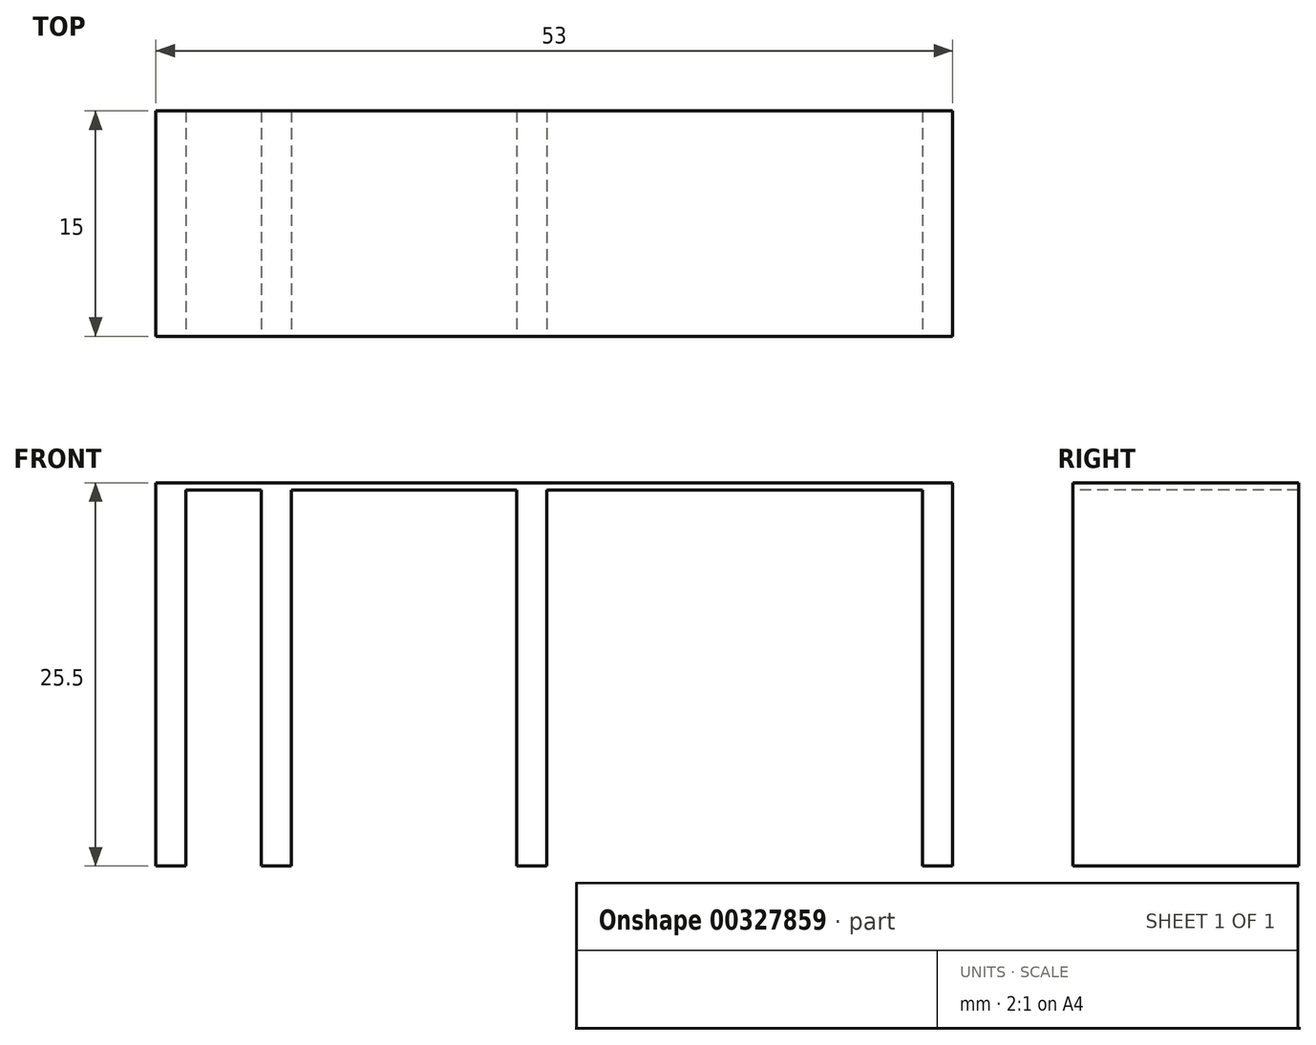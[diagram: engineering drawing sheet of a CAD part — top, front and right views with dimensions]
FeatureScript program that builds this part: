
annotation { "Feature Type Name" : "Feature", "Feature Type Description" : "" }
export const myFeature = defineFeature(function(context is Context, id is Id, definition is map)
    precondition{}
    {
        {
            var Q0;
            Q0=qCreatedBy(makeId("Top.planeOp"),FACE);
            var sketch = newSketch(context, id + "F0", { "sketchPlane" : qUnion([Q0])});
            skLineSegment(sketch, "E0.bottom", {"start": v(-48.72, 7.5) * mm, "end": v(-46.72, 7.5) * mm});
            skLineSegment(sketch, "E0.top", {"start": v(-48.72, -7.5) * mm, "end": v(-46.72, -7.5) * mm});
            skLineSegment(sketch, "E0.left", {"start": v(-48.72, 7.5) * mm, "end": v(-48.72, -7.5) * mm});
            skLineSegment(sketch, "E0.right", {"start": v(-46.72, 7.5) * mm, "end": v(-46.72, -7.5) * mm});
            skLineSegment(sketch, "E1.bottom", {"start": v(-41.72, 7.5) * mm, "end": v(-39.72, 7.5) * mm});
            skLineSegment(sketch, "E1.top", {"start": v(-41.72, -7.5) * mm, "end": v(-39.72, -7.5) * mm});
            skLineSegment(sketch, "E1.left", {"start": v(-41.72, 7.5) * mm, "end": v(-41.72, -7.5) * mm});
            skLineSegment(sketch, "E1.right", {"start": v(-39.72, 7.5) * mm, "end": v(-39.72, -7.5) * mm});
            skLineSegment(sketch, "E2.bottom", {"start": v(-24.72, 7.5) * mm, "end": v(-22.72, 7.5) * mm});
            skLineSegment(sketch, "E2.top", {"start": v(-24.72, -7.5) * mm, "end": v(-22.72, -7.5) * mm});
            skLineSegment(sketch, "E2.left", {"start": v(-24.72, 7.5) * mm, "end": v(-24.72, -7.5) * mm});
            skLineSegment(sketch, "E2.right", {"start": v(-22.72, 7.5) * mm, "end": v(-22.72, -7.5) * mm});
            skLineSegment(sketch, "E3.bottom", {"start": v(2.28, 7.5) * mm, "end": v(4.28, 7.5) * mm});
            skLineSegment(sketch, "E3.top", {"start": v(2.28, -7.5) * mm, "end": v(4.28, -7.5) * mm});
            skLineSegment(sketch, "E3.left", {"start": v(2.28, 7.5) * mm, "end": v(2.28, -7.5) * mm});
            skLineSegment(sketch, "E3.right", {"start": v(4.28, 7.5) * mm, "end": v(4.28, -7.5) * mm});
            skSolve(sketch);
        }
        {
            var Q0;
            Q0 = qSketchRegion(id + "F0", true);
            extrude(context, id + "F1", {"entities" : qUnion([Q0]), "depth" : 25 * mm});
        }
        {
            var Q0;
            Q0=makeQuery(id+"F1.opExtrude","CAP_FACE",FACE,{"disambiguationData":[OSD([sQuery(id+"F0.wireOp",EDGE,"E0.bottom"),sQuery(id+"F0.wireOp",EDGE,"E0.top"),sQuery(id+"F0.wireOp",EDGE,"E0.left"),sQuery(id+"F0.wireOp",EDGE,"E0.right")])],"isStart":false});
            var sketch = newSketch(context, id + "F2", { "sketchPlane" : qUnion([Q0])});
            skLineSegment(sketch, "E4.bottom", {"start": v(-48.72, -7.5) * mm, "end": v(4.28, -7.5) * mm});
            skLineSegment(sketch, "E4.top", {"start": v(-48.72, 7.5) * mm, "end": v(4.28, 7.5) * mm});
            skLineSegment(sketch, "E4.left", {"start": v(-48.72, -7.5) * mm, "end": v(-48.72, 7.5) * mm});
            skLineSegment(sketch, "E4.right", {"start": v(4.28, -7.5) * mm, "end": v(4.28, 7.5) * mm});
            skSolve(sketch);
        }
        {
            var Q0;
            Q0 = qSketchRegion(id + "F2", true);
            extrude(context, id + "F3", {"entities" : qUnion([Q0]), "operationType" : NewBodyOperationType.ADD, "depth" : 0.5 * mm});
        }
    });
